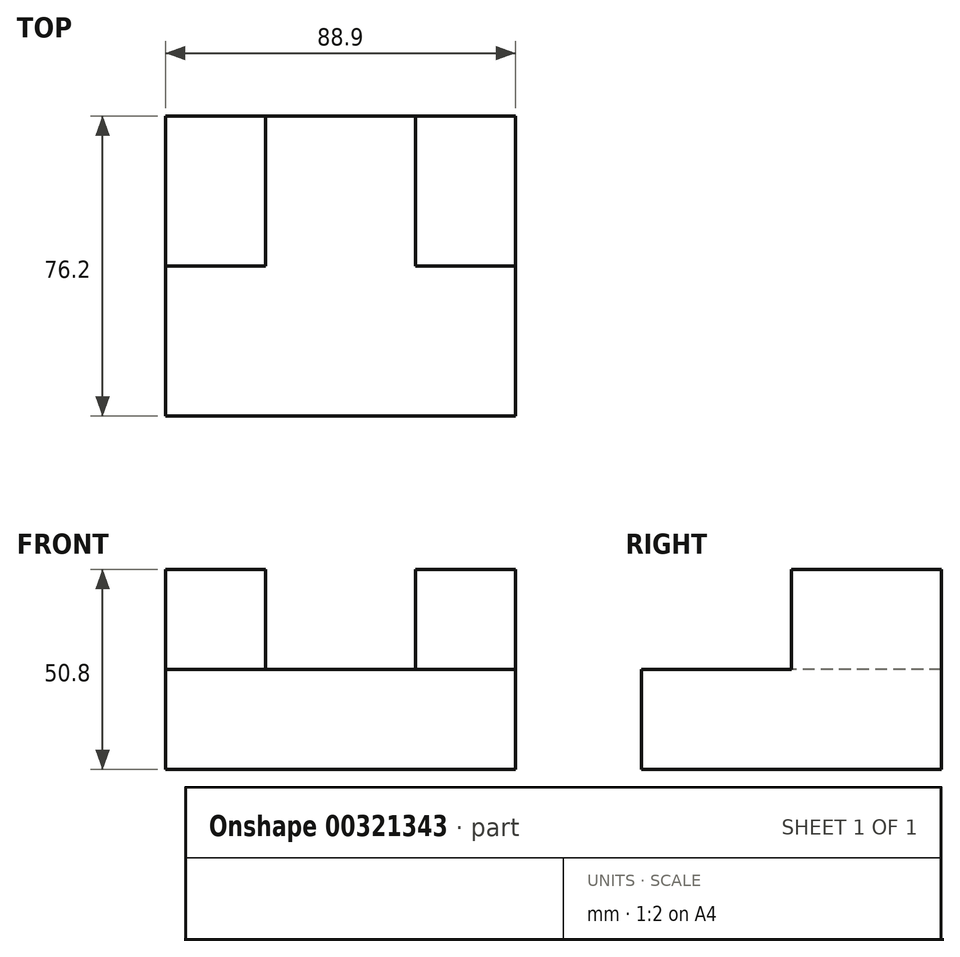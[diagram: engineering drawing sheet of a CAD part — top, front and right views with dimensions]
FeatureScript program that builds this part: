
annotation { "Feature Type Name" : "Feature", "Feature Type Description" : "" }
export const myFeature = defineFeature(function(context is Context, id is Id, definition is map)
    precondition{}
    {
        {
            var Q0;
            Q0=qCreatedBy(makeId("Front.planeOp"),FACE);
            var sketch = newSketch(context, id + "F0", { "sketchPlane" : qUnion([Q0])});
            skLineSegment(sketch, "E0", {"start": v(-44.33, -14.54) * mm, "end": v(44.57, -14.54) * mm});
            skLineSegment(sketch, "E1", {"start": v(44.57, -14.54) * mm, "end": v(44.57, -39.94) * mm});
            skLineSegment(sketch, "E2", {"start": v(44.57, -39.94) * mm, "end": v(-44.33, -39.94) * mm});
            skLineSegment(sketch, "E3", {"start": v(-44.33, -39.94) * mm, "end": v(-44.33, -14.54) * mm});
            skSolve(sketch);
        }
        {
            var Q0;
            Q0 = qSketchRegion(id + "F0", true);
            extrude(context, id + "F1", {"entities" : qUnion([Q0]), "depth" : 76.2 * mm});
        }
        {
            var Q0;
            Q0=makeQuery(id+"F1.opExtrude","SWEPT_FACE",FACE,{"disambiguationData":[OSD([sQuery(id+"F0.wireOp",EDGE,"E0")])]});
            var sketch = newSketch(context, id + "F2", { "sketchPlane" : qUnion([Q0])});
            skLineSegment(sketch, "E4.bottom", {"start": v(-44.33, 0) * mm, "end": v(-18.93, 0) * mm});
            skLineSegment(sketch, "E4.top", {"start": v(-44.33, -38.1) * mm, "end": v(-18.93, -38.1) * mm});
            skLineSegment(sketch, "E4.left", {"start": v(-44.33, 0) * mm, "end": v(-44.33, -38.1) * mm});
            skLineSegment(sketch, "E4.right", {"start": v(-18.93, 0) * mm, "end": v(-18.93, -38.1) * mm});
            skLineSegment(sketch, "E5.bottom", {"start": v(44.57, 0) * mm, "end": v(19.17, 0) * mm});
            skLineSegment(sketch, "E5.top", {"start": v(44.57, -38.1) * mm, "end": v(19.17, -38.1) * mm});
            skLineSegment(sketch, "E5.left", {"start": v(44.57, 0) * mm, "end": v(44.57, -38.1) * mm});
            skLineSegment(sketch, "E5.right", {"start": v(19.17, 0) * mm, "end": v(19.17, -38.1) * mm});
            skSolve(sketch);
        }
        {
            var Q0;
            Q0 = qSketchRegion(id + "F2", true);
            extrude(context, id + "F3", {"entities" : qUnion([Q0]), "operationType" : NewBodyOperationType.ADD, "depth" : 25.4 * mm});
        }
    });
